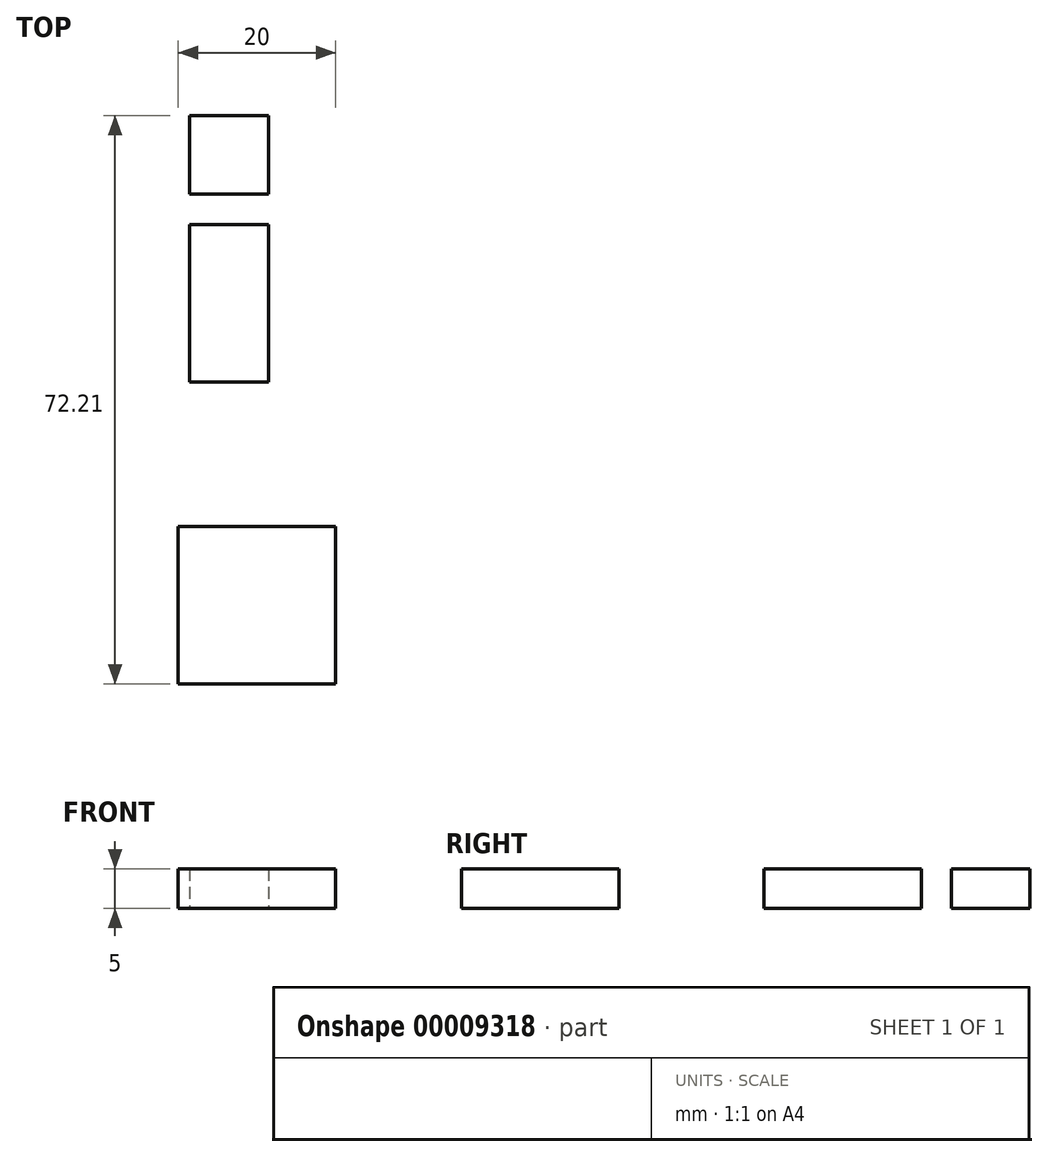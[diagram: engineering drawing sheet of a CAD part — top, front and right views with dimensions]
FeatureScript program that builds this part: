
annotation { "Feature Type Name" : "Feature", "Feature Type Description" : "" }
export const myFeature = defineFeature(function(context is Context, id is Id, definition is map)
    precondition{}
    {
        {
            var Q0;
            Q0=qCreatedBy(makeId("Top.planeOp"),FACE);
            var sketch = newSketch(context, id + "F0", { "sketchPlane" : qUnion([Q0])});
            skLineSegment(sketch, "E0.bottom", {"start": v(-56.65, 44.1) * mm, "end": v(-46.65, 44.1) * mm});
            skLineSegment(sketch, "E0.top", {"start": v(-56.65, 34.1) * mm, "end": v(-46.65, 34.1) * mm});
            skLineSegment(sketch, "E0.left", {"start": v(-56.65, 44.1) * mm, "end": v(-56.65, 34.1) * mm});
            skLineSegment(sketch, "E0.right", {"start": v(-46.65, 44.1) * mm, "end": v(-46.65, 34.1) * mm});
            skLineSegment(sketch, "E1.bottom", {"start": v(-56.65, 30.28) * mm, "end": v(-46.65, 30.28) * mm});
            skLineSegment(sketch, "E1.top", {"start": v(-56.65, 10.28) * mm, "end": v(-46.65, 10.28) * mm});
            skLineSegment(sketch, "E1.left", {"start": v(-56.65, 30.28) * mm, "end": v(-56.65, 10.28) * mm});
            skLineSegment(sketch, "E1.right", {"start": v(-46.65, 30.28) * mm, "end": v(-46.65, 10.28) * mm});
            skLineSegment(sketch, "E2.bottom", {"start": v(-58.12, -8.1) * mm, "end": v(-38.12, -8.1) * mm});
            skLineSegment(sketch, "E2.top", {"start": v(-58.12, -28.1) * mm, "end": v(-38.12, -28.1) * mm});
            skLineSegment(sketch, "E2.left", {"start": v(-58.12, -8.1) * mm, "end": v(-58.12, -28.1) * mm});
            skLineSegment(sketch, "E2.right", {"start": v(-38.12, -8.1) * mm, "end": v(-38.12, -28.1) * mm});
            skSolve(sketch);
        }
        {
            var Q0;
            Q0=makeQuery(id+"F0.imprint","IMPRINT",FACE,{"disambiguationData":[TD([[makeQuery(id+"F0.imprint","IMPRINT",EDGE,{"derivedFrom":sQuery(id+"F0.wireOp",EDGE,"E0.bottom")}),-1.0]])]});
            var Q1;
            Q1=makeQuery(id+"F0.imprint","IMPRINT",FACE,{"disambiguationData":[TD([[makeQuery(id+"F0.imprint","IMPRINT",EDGE,{"derivedFrom":sQuery(id+"F0.wireOp",EDGE,"E1.bottom")}),-1.0]])]});
            var Q2;
            Q2=makeQuery(id+"F0.imprint","IMPRINT",FACE,{"disambiguationData":[TD([[makeQuery(id+"F0.imprint","IMPRINT",EDGE,{"derivedFrom":sQuery(id+"F0.wireOp",EDGE,"E2.bottom")}),-1.0]])]});
            extrude(context, id + "F1", {"entities" : qUnion([Q0, Q1, Q2]), "depth" : 5 * mm});
        }
    });
